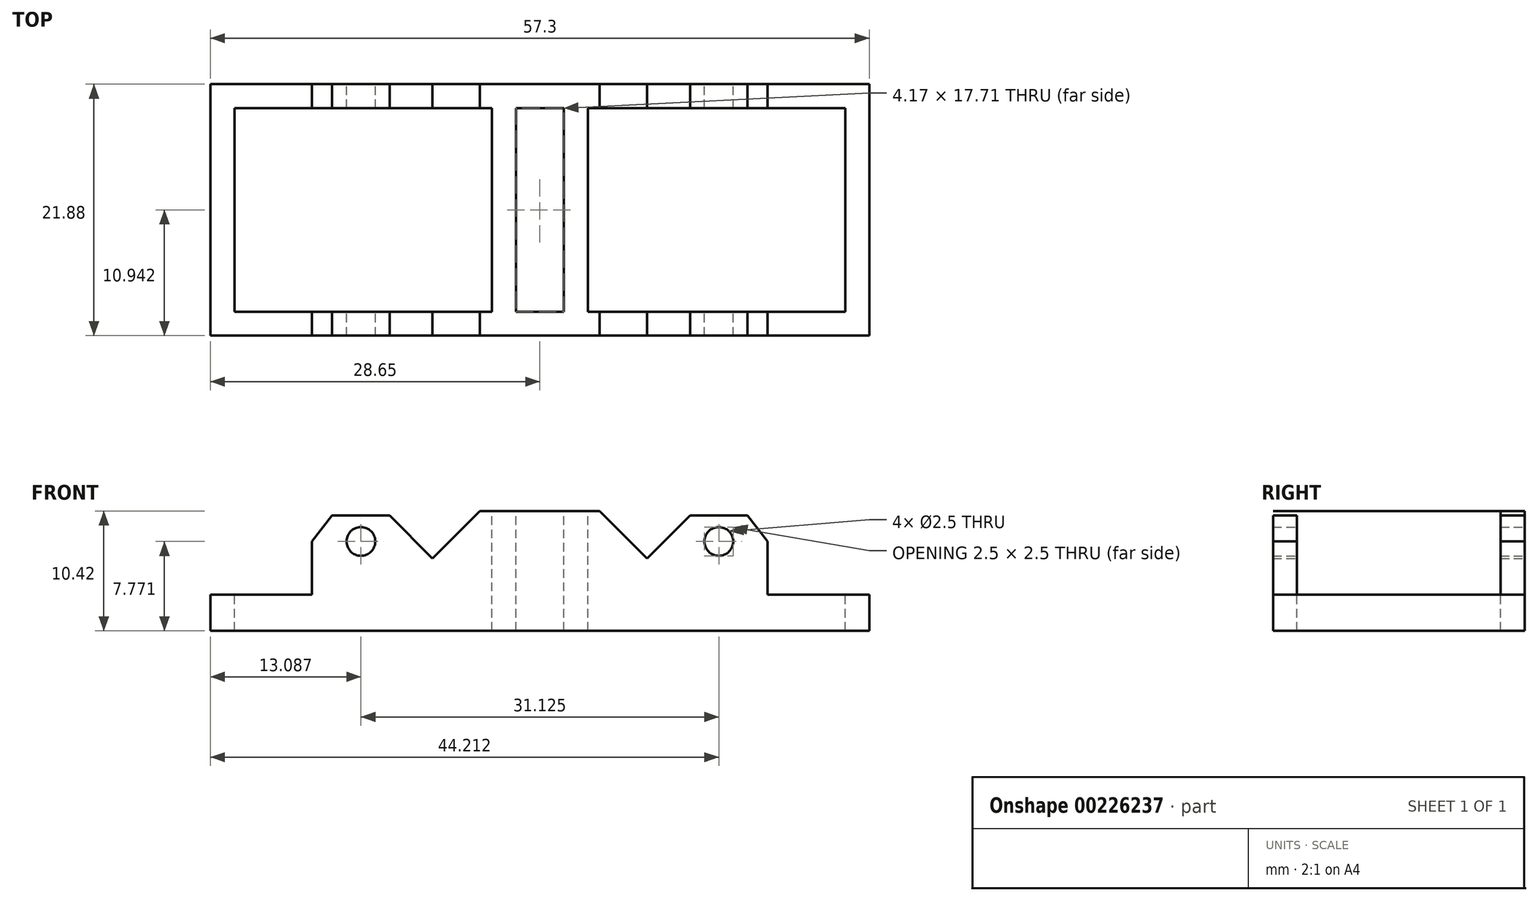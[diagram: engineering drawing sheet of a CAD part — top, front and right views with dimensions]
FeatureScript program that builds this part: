
annotation { "Feature Type Name" : "Feature", "Feature Type Description" : "" }
export const myFeature = defineFeature(function(context is Context, id is Id, definition is map)
    precondition{}
    {
        {
            var Q0;
            Q0=qCreatedBy(makeId("Front.planeOp"),FACE);
            var sketch = newSketch(context, id + "F0", { "sketchPlane" : qUnion([Q0])});
            skLineSegment(sketch, "E0", {"start": v(0, 0) * mm, "end": v(28.65, 0) * mm});
            skLineSegment(sketch, "E1", {"start": v(28.65, 0) * mm, "end": v(28.65, 3.13) * mm});
            skLineSegment(sketch, "E2", {"start": v(28.65, 3.13) * mm, "end": v(12.5, 3.12) * mm});
            skLineSegment(sketch, "E3", {"start": v(12.5, 3.12) * mm, "end": v(5.2, 10.42) * mm});
            skLineSegment(sketch, "E4", {"start": v(5.2, 10.42) * mm, "end": v(0, 10.42) * mm});
            skLineSegment(sketch, "E5", {"start": v(0, 10.42) * mm, "end": v(0, 0) * mm, "construction": true});
            skLineSegment(sketch, "E6", {"start": v(26.04, 3.13) * mm, "end": v(26.04, 0) * mm, "construction": true});
            skLineSegment(sketch, "E7", {"start": v(0, -2.7) * mm, "end": v(28.65, -2.7) * mm, "construction": true});
            skLineSegment(sketch, "E8", {"start": v(28.65, -2.7) * mm, "end": v(28.65, 0) * mm, "construction": true});
            skLineSegment(sketch, "E9", {"start": v(28.65, 3.13) * mm, "end": v(0, 3.13) * mm, "construction": true});
            skCircle(sketch, "E10", {"center": v(15.56, 7.77) * mm, "radius": 10.48 * mm, "construction": true});
            skPoint(sketch, "E11", {"position": v(14.32, 3.13) * mm});
            skLineSegment(sketch, "E12.MirrorCS", {"start": v(-28.65, 3.12) * mm, "end": v(-12.5, 3.12) * mm});
            skPoint(sketch, "E13.MirrorP", {"position": v(-14.32, 3.12) * mm});
            skLineSegment(sketch, "E14.MirrorCS", {"start": v(0, 0) * mm, "end": v(-28.65, 0) * mm});
            skCircle(sketch, "E15.MirrorC", {"center": v(-15.56, 7.77) * mm, "radius": 10.48 * mm, "construction": true});
            skLineSegment(sketch, "E16.MirrorCS", {"start": v(-26.04, 3.12) * mm, "end": v(-26.04, 0) * mm, "construction": true});
            skLineSegment(sketch, "E17.MirrorCS", {"start": v(-28.65, -2.7) * mm, "end": v(-28.65, 0) * mm, "construction": true});
            skLineSegment(sketch, "E18.MirrorCS", {"start": v(-28.65, 0) * mm, "end": v(-28.65, 3.12) * mm});
            skLineSegment(sketch, "E19.MirrorCS", {"start": v(-5.2, 10.42) * mm, "end": v(0, 10.42) * mm});
            skLineSegment(sketch, "E20.MirrorCS", {"start": v(0, -2.7) * mm, "end": v(-28.65, -2.7) * mm, "construction": true});
            skLineSegment(sketch, "E21.MirrorCS", {"start": v(-28.65, 3.12) * mm, "end": v(0, 3.13) * mm, "construction": true});
            skLineSegment(sketch, "E22.MirrorCS", {"start": v(-12.5, 3.12) * mm, "end": v(-5.2, 10.42) * mm});
            skCircle(sketch, "E23", {"center": v(15.56, 7.77) * mm, "radius": 1.25 * mm});
            skLineSegment(sketch, "E24", {"start": v(13.06, 10.02) * mm, "end": v(18.06, 10.02) * mm});
            skLineSegment(sketch, "E25", {"start": v(18.06, 10.02) * mm, "end": v(19.81, 7.77) * mm});
            skLineSegment(sketch, "E26", {"start": v(19.81, 7.77) * mm, "end": v(19.81, 3.12) * mm});
            skLineSegment(sketch, "E27", {"start": v(15.56, 7.77) * mm, "end": v(15.56, 10.02) * mm, "construction": true});
            skLineSegment(sketch, "E28.MirrorCS", {"start": v(-19.81, 7.77) * mm, "end": v(-19.81, 3.12) * mm});
            skLineSegment(sketch, "E29.MirrorCS", {"start": v(-18.06, 10.02) * mm, "end": v(-19.81, 7.77) * mm});
            skLineSegment(sketch, "E30.MirrorCS", {"start": v(-13.06, 10.02) * mm, "end": v(-18.06, 10.02) * mm});
            skCircle(sketch, "E31", {"center": v(-15.56, 7.77) * mm, "radius": 1.25 * mm});
            skLineSegment(sketch, "E32", {"start": v(13.06, 10.02) * mm, "end": v(9.33, 6.3) * mm});
            skLineSegment(sketch, "E33", {"start": v(-13.06, 10.02) * mm, "end": v(-9.33, 6.3) * mm});
            skSolve(sketch);
        }
        {
            var Q0;
            Q0 = qSketchRegion(id + "F0", true);
            extrude(context, id + "F1", {"entities" : qUnion([Q0]), "depth" : (1050 / 48) * mm});
        }
        {
            var Q0;
            Q0=makeQuery(id+"F1.opExtrude","SWEPT_FACE",FACE,{"disambiguationData":[OSD([sQuery(id+"F0.wireOp",EDGE,"E4"),sQuery(id+"F0.wireOp",EDGE,"E19.MirrorCS")])]});
            var sketch = newSketch(context, id + "F2", { "sketchPlane" : qUnion([Q0])});
            skLineSegment(sketch, "E34.bottom", {"start": v(-28.65, 0) * mm, "end": v(28.65, 0) * mm, "construction": true});
            skLineSegment(sketch, "E34.top", {"start": v(-28.65, -21.88) * mm, "end": v(28.65, -21.87) * mm, "construction": true});
            skLineSegment(sketch, "E34.left", {"start": v(-28.65, 0) * mm, "end": v(-28.65, -21.88) * mm, "construction": true});
            skLineSegment(sketch, "E34.right", {"start": v(28.65, 0) * mm, "end": v(28.65, -21.88) * mm, "construction": true});
            skLineSegment(sketch, "E35", {"start": v(-28.65, -2.08) * mm, "end": v(28.65, -2.08) * mm, "construction": true});
            skLineSegment(sketch, "E36", {"start": v(28.65, -2.08) * mm, "end": v(28.65, -19.8) * mm, "construction": true});
            skLineSegment(sketch, "E37", {"start": v(28.65, -19.8) * mm, "end": v(-28.65, -19.8) * mm, "construction": true});
            skLineSegment(sketch, "E38", {"start": v(-26.56, 0) * mm, "end": v(-26.56, -21.88) * mm, "construction": true});
            skLineSegment(sketch, "E39", {"start": v(26.56, 0) * mm, "end": v(26.56, -21.87) * mm, "construction": true});
            skLineSegment(sketch, "E40", {"start": v(-26.56, -2.08) * mm, "end": v(-4.17, -2.08) * mm});
            skLineSegment(sketch, "E41", {"start": v(-4.17, -2.08) * mm, "end": v(-4.17, -19.8) * mm});
            skLineSegment(sketch, "E42", {"start": v(-4.17, -19.8) * mm, "end": v(-26.56, -19.8) * mm});
            skLineSegment(sketch, "E43", {"start": v(-26.56, -19.8) * mm, "end": v(-26.56, -2.08) * mm});
            skLineSegment(sketch, "E44", {"start": v(4.17, -2.08) * mm, "end": v(26.56, -2.08) * mm});
            skLineSegment(sketch, "E45", {"start": v(26.56, -2.08) * mm, "end": v(26.56, -19.8) * mm});
            skLineSegment(sketch, "E46", {"start": v(26.56, -19.8) * mm, "end": v(4.17, -19.8) * mm});
            skLineSegment(sketch, "E47", {"start": v(4.17, -19.8) * mm, "end": v(4.17, -2.08) * mm});
            skLineSegment(sketch, "E48", {"start": v(0, 0) * mm, "end": v(0, -21.88) * mm, "construction": true});
            skLineSegment(sketch, "E49.bottom", {"start": v(-2.08, -2.08) * mm, "end": v(2.08, -2.08) * mm});
            skLineSegment(sketch, "E49.top", {"start": v(-2.08, -19.8) * mm, "end": v(2.08, -19.8) * mm});
            skLineSegment(sketch, "E49.left", {"start": v(-2.08, -2.08) * mm, "end": v(-2.08, -19.8) * mm});
            skLineSegment(sketch, "E49.right", {"start": v(2.08, -2.08) * mm, "end": v(2.08, -19.8) * mm});
            skSolve(sketch);
        }
        {
            var Q0;
            Q0 = qSketchRegion(id + "F2", true);
            extrude(context, id + "F3", {"entities" : qUnion([Q0]), "operationType" : NewBodyOperationType.REMOVE, "endBound" : BoundingType.THROUGH_ALL, "oppositeDirection" : true, "depth" : 25 * mm});
        }
    });
